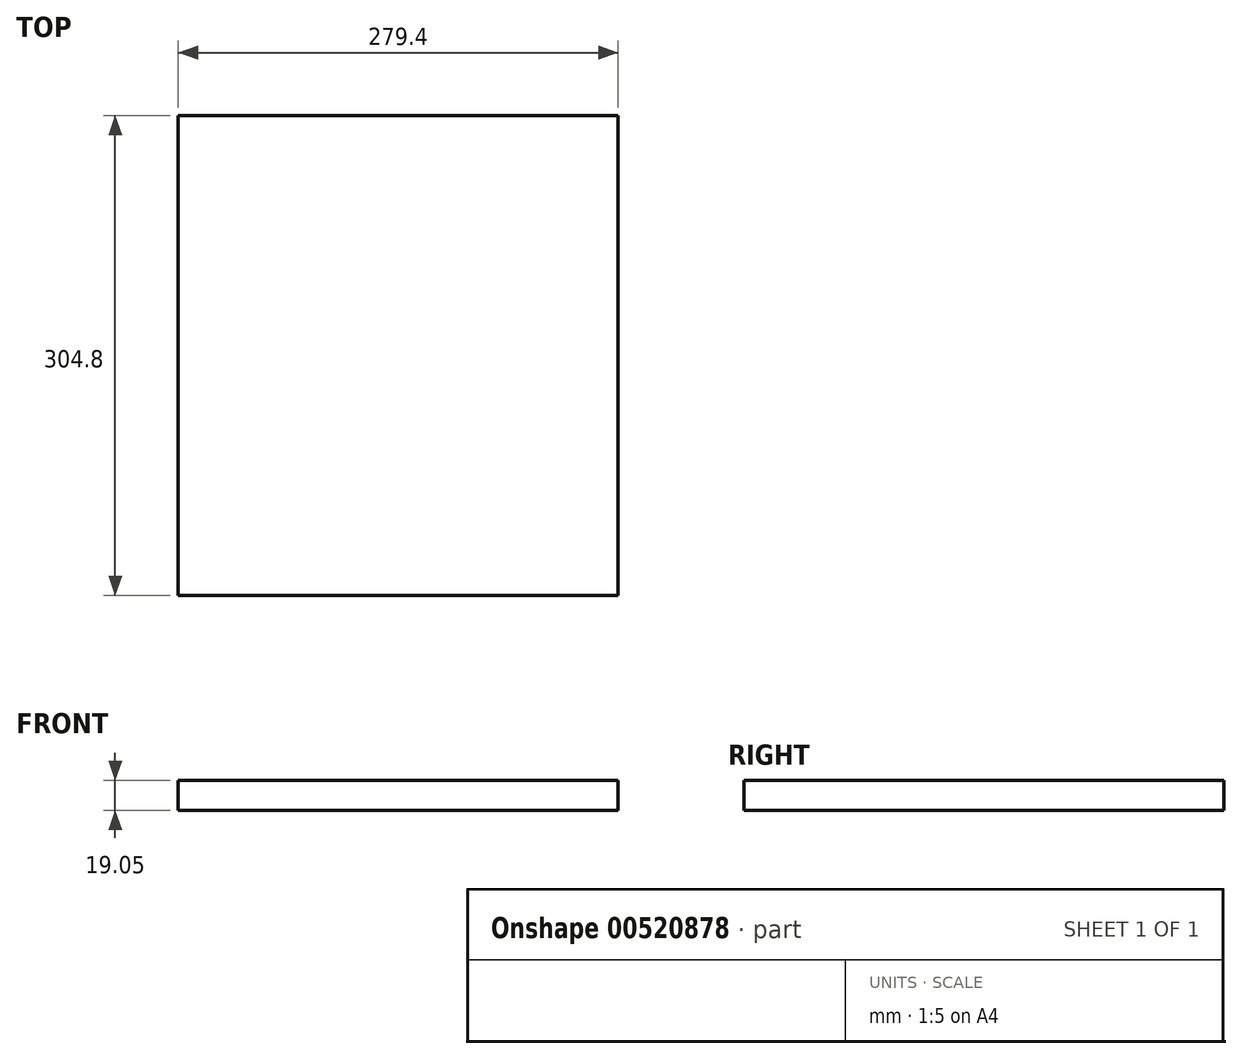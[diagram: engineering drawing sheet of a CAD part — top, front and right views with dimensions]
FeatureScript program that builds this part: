
annotation { "Feature Type Name" : "Feature", "Feature Type Description" : "" }
export const myFeature = defineFeature(function(context is Context, id is Id, definition is map)
    precondition{}
    {
        {
            var Q0;
            Q0=qCreatedBy(makeId("Top.planeOp"),FACE);
            var sketch = newSketch(context, id + "F0", { "sketchPlane" : qUnion([Q0])});
            skLineSegment(sketch, "E0.bottom", {"start": v(139.7, 152.4) * mm, "end": v(-139.7, 152.4) * mm});
            skLineSegment(sketch, "E0.top", {"start": v(139.7, -152.4) * mm, "end": v(-139.7, -152.4) * mm});
            skLineSegment(sketch, "E0.left", {"start": v(139.7, 152.4) * mm, "end": v(139.7, -152.4) * mm});
            skLineSegment(sketch, "E0.right", {"start": v(-139.7, 152.4) * mm, "end": v(-139.7, -152.4) * mm});
            skPoint(sketch, "E0.middle", {"position": v(0, 0) * mm});
            skSolve(sketch);
        }
        {
            var Q0;
            Q0 = qSketchRegion(id + "F0", true);
            extrude(context, id + "F1", {"entities" : qUnion([Q0]), "depth" : 19.05 * mm, "offsetDistance" : 25.4 * mm});
        }
    });
